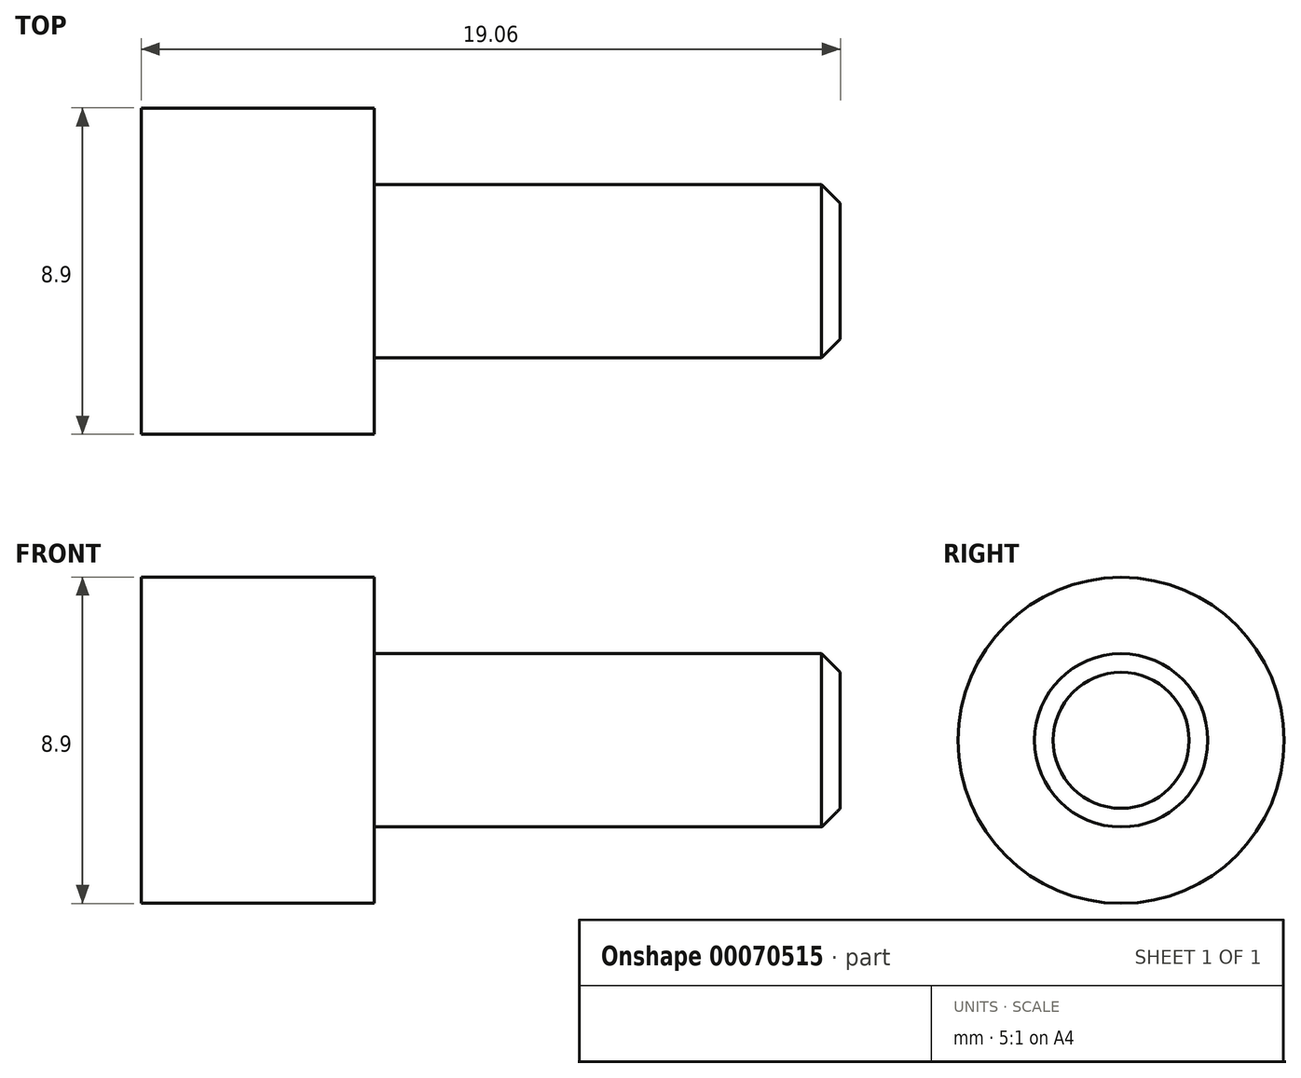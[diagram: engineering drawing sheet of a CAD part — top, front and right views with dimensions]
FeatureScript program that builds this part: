
annotation { "Feature Type Name" : "Feature", "Feature Type Description" : "" }
export const myFeature = defineFeature(function(context is Context, id is Id, definition is map)
    precondition{}
    {
        {
            var Q0;
            Q0=qCreatedBy(makeId("Right.planeOp"),FACE);
            var sketch = newSketch(context, id + "F0", { "sketchPlane" : qUnion([Q0])});
            skCircle(sketch, "E0", {"center": v(0, 0) * mm, "radius": 2.36 * mm});
            skSolve(sketch);
        }
        {
            var Q0;
            Q0=makeQuery(id+"F0.imprint","IMPRINT",FACE,{"disambiguationData":[TD([[makeQuery(id+"F0.imprint","IMPRINT",EDGE,{"derivedFrom":sQuery(id+"F0.wireOp",EDGE,"E0")}),1.0]])]});
            extrude(context, id + "F1", {"entities" : qUnion([Q0]), "endBound" : BoundingType.SYMMETRIC, "depth" : 19.05 * mm});
        }
        {
            var Q0;
            Q0=makeQuery(id+"F1.opExtrude","CAP_FACE",FACE,{"disambiguationData":[OSD([sQuery(id+"F0.wireOp",EDGE,"E0")])],"isStart":true});
            var sketch = newSketch(context, id + "F2", { "sketchPlane" : qUnion([Q0])});
            skCircle(sketch, "E1", {"center": v(0, 0) * mm, "radius": 4.45 * mm});
            skSolve(sketch);
        }
        {
            var Q0;
            Q0=makeQuery(id+"F2.imprint","IMPRINT",FACE,{"disambiguationData":[TD([[makeQuery(id+"F2.imprint","IMPRINT",EDGE,{"derivedFrom":sQuery(id+"F2.wireOp",EDGE,"E1")}),1.0]])]});
            extrude(context, id + "F3", {"entities" : qUnion([Q0]), "operationType" : NewBodyOperationType.ADD, "oppositeDirection" : true, "depth" : 6.35 * mm});
        }
        {
            var Q0;
            Q0=makeQuery(id+"F1.opExtrude","CAP_EDGE",EDGE,{"disambiguationData":[OSD([sQuery(id+"F0.wireOp",EDGE,"E0")])],"isStart":false});
            chamfer(context, id + "F4", {"entities" : qUnion([Q0]), "width" : 0.5 * mm, "tangentPropagation" : true});
        }
    });
